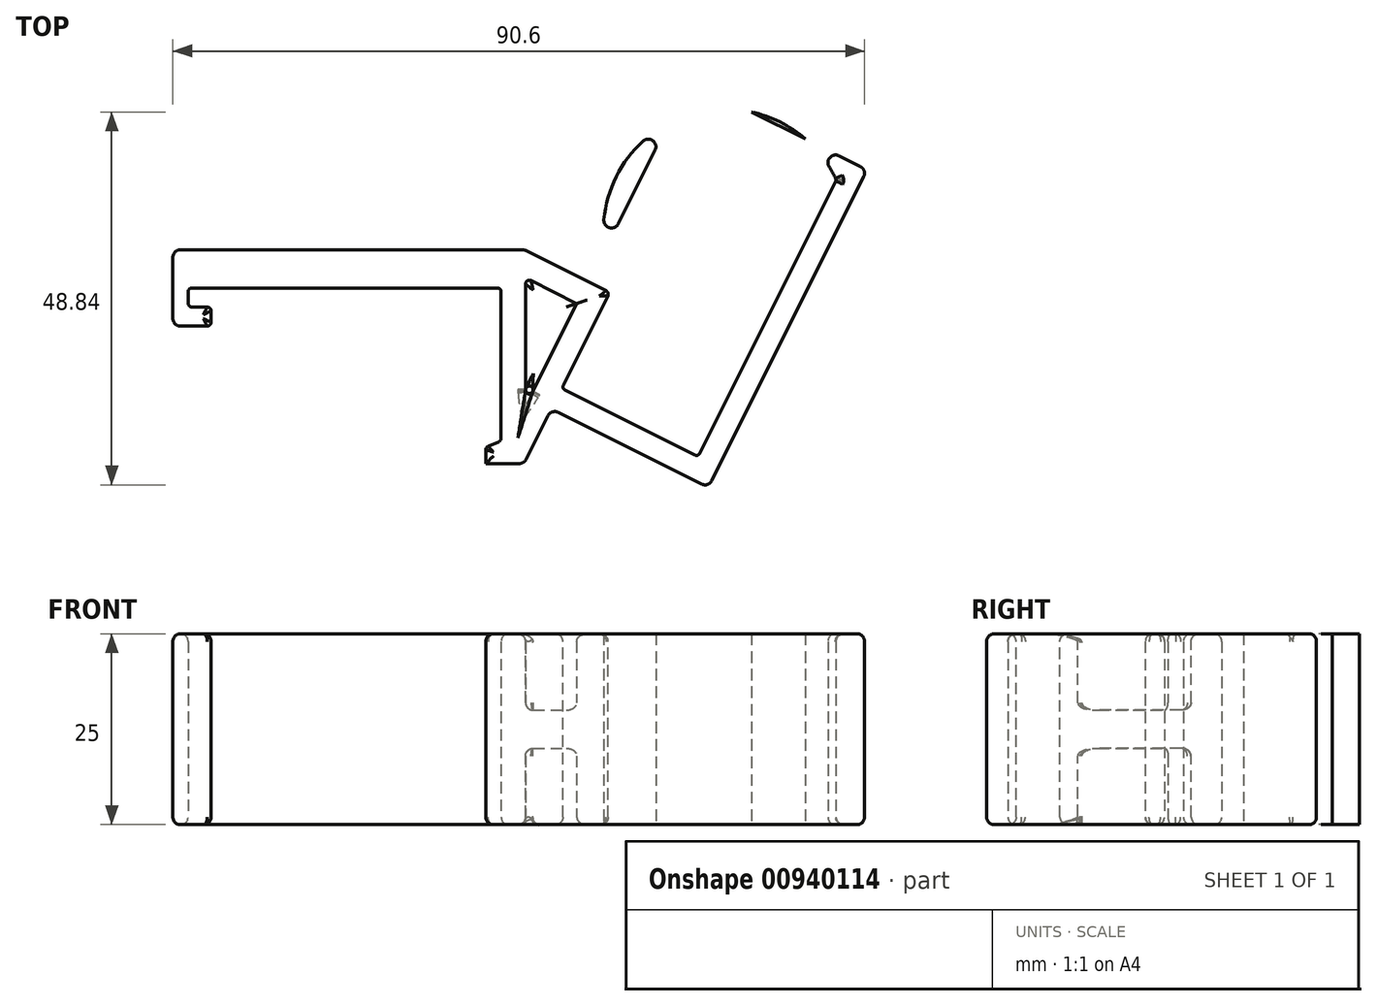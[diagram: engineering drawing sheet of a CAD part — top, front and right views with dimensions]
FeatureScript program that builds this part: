
annotation { "Feature Type Name" : "Feature", "Feature Type Description" : "" }
export const myFeature = defineFeature(function(context is Context, id is Id, definition is map)
    precondition{}
    {
        {
            var Q0;
            Q0=qCreatedBy(makeId("Top.planeOp"),FACE);
            var sketch = newSketch(context, id + "F0", { "sketchPlane" : qUnion([Q0])});
            skLineSegment(sketch, "E0.bottom", {"start": v(0, 0) * mm, "end": v(41, 0) * mm});
            skLineSegment(sketch, "E0.top", {"start": v(0, 2) * mm, "end": v(41, 2) * mm});
            skLineSegment(sketch, "E0.left", {"start": v(0, 0) * mm, "end": v(0, 2) * mm});
            skLineSegment(sketch, "E0.right", {"start": v(41, 0) * mm, "end": v(41, 2) * mm});
            skLineSegment(sketch, "E1.bottom", {"start": v(0, 2) * mm, "end": v(-2, 2) * mm});
            skLineSegment(sketch, "E1.top", {"start": v(0, -2.5) * mm, "end": v(-2, -2.5) * mm});
            skLineSegment(sketch, "E1.left", {"start": v(0, 2) * mm, "end": v(0, -2.5) * mm});
            skLineSegment(sketch, "E1.right", {"start": v(-2, 2) * mm, "end": v(-2, -2.5) * mm});
            skLineSegment(sketch, "E2.bottom", {"start": v(-2, -2.5) * mm, "end": v(3, -2.5) * mm});
            skLineSegment(sketch, "E2.top", {"start": v(-2, -5) * mm, "end": v(3, -5) * mm});
            skLineSegment(sketch, "E2.left", {"start": v(-2, -2.5) * mm, "end": v(-2, -5) * mm});
            skLineSegment(sketch, "E2.right", {"start": v(3, -2.5) * mm, "end": v(3, -5) * mm});
            skLineSegment(sketch, "E3.bottom", {"start": v(41, 2) * mm, "end": v(44, 2) * mm});
            skLineSegment(sketch, "E3.top", {"start": v(41, -23) * mm, "end": v(44, -23) * mm});
            skLineSegment(sketch, "E3.left", {"start": v(41, 2) * mm, "end": v(41, -23) * mm});
            skLineSegment(sketch, "E3.right", {"start": v(44, 2) * mm, "end": v(44, -23) * mm});
            skLineSegment(sketch, "E4.bottom", {"start": v(41, -23) * mm, "end": v(39, -23) * mm});
            skLineSegment(sketch, "E4.top", {"start": v(41, -20) * mm, "end": v(39, -20) * mm});
            skLineSegment(sketch, "E4.left", {"start": v(41, -23) * mm, "end": v(41, -20) * mm});
            skLineSegment(sketch, "E4.right", {"start": v(39, -23) * mm, "end": v(39, -20) * mm});
            skLineSegment(sketch, "E5.bottom", {"start": v(39, -23) * mm, "end": v(37.5, -23) * mm});
            skLineSegment(sketch, "E5.top", {"start": v(39, -13) * mm, "end": v(37.5, -13) * mm});
            skLineSegment(sketch, "E5.left", {"start": v(39, -23) * mm, "end": v(39, -13) * mm});
            skLineSegment(sketch, "E5.right", {"start": v(37.5, -23) * mm, "end": v(37.5, -13) * mm});
            skLineSegment(sketch, "E6.bottom", {"start": v(-2, 2) * mm, "end": v(44, 2) * mm});
            skLineSegment(sketch, "E6.top", {"start": v(-2, 5) * mm, "end": v(44, 5) * mm});
            skLineSegment(sketch, "E6.left", {"start": v(-2, 2) * mm, "end": v(-2, 5) * mm});
            skLineSegment(sketch, "E6.right", {"start": v(44, 2) * mm, "end": v(44, 5) * mm});
            skLineSegment(sketch, "E7", {"start": v(44, 5) * mm, "end": v(28, 14) * mm});
            skLineSegment(sketch, "E8", {"start": v(28, 14) * mm, "end": v(-2, 5) * mm});
            skLineSegment(sketch, "E9", {"start": v(28, 14) * mm, "end": v(28, 5) * mm});
            skLineSegment(sketch, "E10.bottom", {"start": v(37.5, -23) * mm, "end": v(39, -23) * mm});
            skLineSegment(sketch, "E10.top", {"start": v(37.5, -20) * mm, "end": v(39, -20) * mm});
            skLineSegment(sketch, "E10.left", {"start": v(37.5, -23) * mm, "end": v(37.5, -20) * mm});
            skLineSegment(sketch, "E11.bottom", {"start": v(44, 5) * mm, "end": v(28, 5) * mm});
            skLineSegment(sketch, "E11.top", {"start": v(44, 14) * mm, "end": v(28, 14) * mm});
            skLineSegment(sketch, "E11.left", {"start": v(44, 5) * mm, "end": v(44, 14) * mm});
            skLineSegment(sketch, "E11.right", {"start": v(28, 5) * mm, "end": v(28, 14) * mm});
            skLineSegment(sketch, "E12.bottom", {"start": v(-2, 5) * mm, "end": v(28, 5) * mm});
            skLineSegment(sketch, "E12.top", {"start": v(-2, 14) * mm, "end": v(28, 14) * mm});
            skLineSegment(sketch, "E12.left", {"start": v(-2, 5) * mm, "end": v(-2, 14) * mm});
            skLineSegment(sketch, "E13", {"start": v(44, -23) * mm, "end": v(55.2, -0.6) * mm});
            skLineSegment(sketch, "E14", {"start": v(37.5, -21.5) * mm, "end": v(41, -20) * mm});
            skLineSegment(sketch, "E15", {"start": v(44, 5) * mm, "end": v(55.2, -0.6) * mm});
            skLineSegment(sketch, "E16", {"start": v(57.86, -17.63) * mm, "end": v(70.39, 7.41) * mm});
            skCircle(sketch, "E17", {"center": v(70.39, 7.41) * mm, "radius": 16 * mm});
            skLineSegment(sketch, "E18", {"start": v(55.2, -0.6) * mm, "end": v(67.03, 23.06) * mm});
            skLineSegment(sketch, "E19", {"start": v(57.86, -17.63) * mm, "end": v(48.92, -13.16) * mm});
            skLineSegment(sketch, "E20", {"start": v(67.03, 23.06) * mm, "end": v(84.9, 14.12) * mm});
            skLineSegment(sketch, "E21", {"start": v(84.9, 14.12) * mm, "end": v(66.8, -22.1) * mm});
            skLineSegment(sketch, "E22", {"start": v(66.8, -22.1) * mm, "end": v(57.86, -17.63) * mm});
            skLineSegment(sketch, "E23", {"start": v(47.58, -15.84) * mm, "end": v(68.15, -26.13) * mm});
            skLineSegment(sketch, "E24", {"start": v(68.15, -26.13) * mm, "end": v(88.94, 15.46) * mm});
            skLineSegment(sketch, "E25", {"start": v(88.94, 15.46) * mm, "end": v(65.69, 27.09) * mm});
            skPoint(sketch, "E26", {"position": v(55.2, -0.6) * mm});
            skPoint(sketch, "E27", {"position": v(52.52, 0.74) * mm});
            skLineSegment(sketch, "E28", {"start": v(52.52, 0.74) * mm, "end": v(65.69, 27.09) * mm});
            skSolve(sketch);
        }
        {
            var Q0;
            Q0=makeQuery(id+"F0.imprint","IMPRINT",FACE,{"disambiguationData":[TD([[makeQuery(id+"F0.imprint","IMPRINT",EDGE,{"derivedFrom":sQuery(id+"F0.wireOp",EDGE,"E2.top")}),1.0]])]});
            var Q1;
            Q1=makeQuery(id+"F0.imprint","IMPRINT",FACE,{"disambiguationData":[TD([[makeQuery(id+"F0.imprint","IMPRINT",EDGE,{"derivedFrom":sQuery(id+"F0.wireOp",EDGE,"E4.bottom")}),-1.0]])]});
            var Q2;
            Q2=makeQuery(id+"F0.imprint","IMPRINT",FACE,{"disambiguationData":[TD([[makeQuery(id+"F0.imprint","IMPRINT",EDGE,{"derivedFrom":sQuery(id+"F0.wireOp",EDGE,"E10.bottom")}),1.0]])]});
            var Q3;
            {var subQ0=sQuery(id+"F0.wireOp",EDGE,"E6.left");Q3=makeQuery(id+"F0.imprint","IMPRINT",FACE,{"disambiguationData":[TD([[makeQuery(id+"F0.imprint","IMPRINT",EDGE,{"derivedFrom":subQ0}),-1.0]])]});}
            var Q4;
            Q4=makeQuery(id+"F0.imprint","IMPRINT",FACE,{"disambiguationData":[TD([[makeQuery(id+"F0.imprint","IMPRINT",EDGE,{"derivedFrom":sQuery(id+"F0.wireOp",EDGE,"E3.right")}),1.0]])]});
            var Q5;
            Q5=makeQuery(id+"F0.imprint","IMPRINT",FACE,{"disambiguationData":[TD([[makeQuery(id+"F0.imprint","IMPRINT",EDGE,{"derivedFrom":sQuery(id+"F0.wireOp",EDGE,"E3.top")}),1.0]])]});
            var Q6;
            {var subQ4=sQuery(id+"F0.wireOp",EDGE,"JwhKLXGQ-pJKR-nMGy-SPGt-QLhxBQO2lQYZ");var subQ6=sQuery(id+"F0.wireOp",EDGE,"E13");var subQ7=makeQuery(id+"F0.imprint","INTERSECT",VERTEX,{"derivedFrom":[subQ4,subQ6]});Q6=makeQuery(id+"F0.imprint","IMPRINT",FACE,{"disambiguationData":[TD([[makeQuery(id+"F0.imprint","IMPRINT",EDGE,{"disambiguationData":[TD([[subQ7,1.0]])],"derivedFrom":subQ6}),1.0]])]});}
            var Q7;
            {var subQ3=sQuery(id+"F0.wireOp",EDGE,"E1.right");Q7=makeQuery(id+"F0.imprint","IMPRINT",FACE,{"disambiguationData":[TD([[makeQuery(id+"F0.imprint","IMPRINT",EDGE,{"derivedFrom":subQ3}),1.0]])]});}
            var Q8;
            {var subQ0=sQuery(id+"F0.wireOp",EDGE,"E0.bottom");Q8=makeQuery(id+"F0.imprint","IMPRINT",FACE,{"disambiguationData":[TD([[makeQuery(id+"F0.imprint","IMPRINT",EDGE,{"derivedFrom":subQ0}),1.0]])]});}
            var Q9;
            {var subQ4=sQuery(id+"F0.wireOp",EDGE,"E19");Q9=makeQuery(id+"F0.imprint","IMPRINT",FACE,{"disambiguationData":[TD([[makeQuery(id+"F0.imprint","IMPRINT",EDGE,{"derivedFrom":subQ4}),1.0]])]});}
            var Q10;
            {var subQ1=sQuery(id+"F0.wireOp",EDGE,"E17");var subQ3=sQuery(id+"F0.wireOp",EDGE,"E24");var subQ5=makeQuery(id+"F0.imprint","INTERSECT",VERTEX,{"disambiguationData":[OD(1.0)],"derivedFrom":[subQ1,subQ3]});Q10=makeQuery(id+"F0.imprint","IMPRINT",FACE,{"disambiguationData":[TD([[makeQuery(id+"F0.imprint","IMPRINT",EDGE,{"disambiguationData":[TD([[subQ5,1.0]])],"derivedFrom":subQ1}),1.0]])]});}
            var Q11;
            {var subQ2=sQuery(id+"F0.wireOp",EDGE,"E24");var subQ4=sQuery(id+"F0.wireOp",EDGE,"E25");var subQ5=makeQuery(id+"F0.imprint","INTERSECT",VERTEX,{"derivedFrom":[subQ2,subQ4]});Q11=makeQuery(id+"F0.imprint","IMPRINT",FACE,{"disambiguationData":[TD([[makeQuery(id+"F0.imprint","IMPRINT",EDGE,{"disambiguationData":[TD([[subQ5,1.0]])],"derivedFrom":subQ2}),1.0]])]});}
            var Q12;
            {var subQ1=sQuery(id+"F0.wireOp",EDGE,"E17");var subQ3=sQuery(id+"F0.wireOp",EDGE,"E25");var subQ5=makeQuery(id+"F0.imprint","INTERSECT",VERTEX,{"disambiguationData":[OD(1.0)],"derivedFrom":[subQ1,subQ3]});Q12=makeQuery(id+"F0.imprint","IMPRINT",FACE,{"disambiguationData":[TD([[makeQuery(id+"F0.imprint","IMPRINT",EDGE,{"disambiguationData":[TD([[subQ5,-1.0]])],"derivedFrom":subQ1}),1.0]])]});}
            var Q13;
            {var subQ3=sQuery(id+"F0.wireOp",EDGE,"E17");var subQ8=sQuery(id+"F0.wireOp",EDGE,"E25");var subQ10=makeQuery(id+"F0.imprint","INTERSECT",VERTEX,{"disambiguationData":[OD(1.0)],"derivedFrom":[subQ3,subQ8]});Q13=makeQuery(id+"F0.imprint","IMPRINT",FACE,{"disambiguationData":[TD([[makeQuery(id+"F0.imprint","IMPRINT",EDGE,{"disambiguationData":[TD([[subQ10,-1.0]])],"derivedFrom":subQ3}),-1.0]])]});}
            var Q14;
            {var subQ0=sQuery(id+"F0.wireOp",EDGE,"E28");var subQ1=sQuery(id+"F0.wireOp",EDGE,"E17");var subQ2=makeQuery(id+"F0.imprint","INTERSECT",VERTEX,{"disambiguationData":[OD(0.0)],"derivedFrom":[subQ1,subQ0]});Q14=makeQuery(id+"F0.imprint","IMPRINT",FACE,{"disambiguationData":[TD([[makeQuery(id+"F0.imprint","IMPRINT",EDGE,{"disambiguationData":[TD([[subQ2,1.0]])],"derivedFrom":subQ1}),1.0]])]});}
            var Q15;
            {var subQ3=sQuery(id+"F0.wireOp",EDGE,"E28");var subQ5=sQuery(id+"F0.wireOp",EDGE,"E17");var subQ6=makeQuery(id+"F0.imprint","INTERSECT",VERTEX,{"disambiguationData":[OD(1.0)],"derivedFrom":[subQ5,subQ3]});Q15=makeQuery(id+"F0.imprint","IMPRINT",FACE,{"disambiguationData":[TD([[makeQuery(id+"F0.imprint","IMPRINT",EDGE,{"disambiguationData":[TD([[subQ6,-1.0]])],"derivedFrom":subQ5}),-1.0]])]});}
            extrude(context, id + "F1", {"entities" : qUnion([Q0, Q1, Q2, Q3, Q4, Q5, Q6, Q7, Q8, Q9, Q10, Q11, Q12, Q13, Q14, Q15]), "depth" : 12.5 * mm, "offsetDistance" : 25 * mm, "hasSecondDirection" : true, "secondDirectionOppositeDirection" : true, "secondDirectionDepth" : 12.5 * mm});
        }
        {
            var Q0;
            Q0=makeQuery(id+"F1.opExtrude","CAP_FACE",FACE,{"disambiguationData":[OSD([sQuery(id+"F0.wireOp",EDGE,"E1.left"),sQuery(id+"F0.wireOp",EDGE,"E1.right"),sQuery(id+"F0.wireOp",EDGE,"E2.bottom"),sQuery(id+"F0.wireOp",EDGE,"E2.top"),sQuery(id+"F0.wireOp",EDGE,"E2.left"),sQuery(id+"F0.wireOp",EDGE,"E2.right"),sQuery(id+"F0.wireOp",EDGE,"E3.top"),sQuery(id+"F0.wireOp",EDGE,"E3.left"),sQuery(id+"F0.wireOp",EDGE,"E4.bottom"),sQuery(id+"F0.wireOp",EDGE,"E4.top"),sQuery(id+"F0.wireOp",EDGE,"E6.bottom"),sQuery(id+"F0.wireOp",EDGE,"E6.left"),sQuery(id+"F0.wireOp",EDGE,"E7"),sQuery(id+"F0.wireOp",EDGE,"E8"),sQuery(id+"F0.wireOp",EDGE,"E10.bottom"),sQuery(id+"F0.wireOp",EDGE,"E10.top"),sQuery(id+"F0.wireOp",EDGE,"E10.left"),sQuery(id+"F0.wireOp",EDGE,"JwhKLXGQ-pJKR-nMGy-SPGt-QLhxBQO2lQYZ"),sQuery(id+"F0.wireOp",EDGE,"E13")])],"isStart":false});
            var Q1;
            Q1=makeQuery(id+"F1.opExtrude","CAP_FACE",FACE,{"disambiguationData":[OSD([sQuery(id+"F0.wireOp",EDGE,"E1.left"),sQuery(id+"F0.wireOp",EDGE,"E1.right"),sQuery(id+"F0.wireOp",EDGE,"E2.bottom"),sQuery(id+"F0.wireOp",EDGE,"E2.top"),sQuery(id+"F0.wireOp",EDGE,"E2.left"),sQuery(id+"F0.wireOp",EDGE,"E2.right"),sQuery(id+"F0.wireOp",EDGE,"E3.top"),sQuery(id+"F0.wireOp",EDGE,"E3.left"),sQuery(id+"F0.wireOp",EDGE,"E4.bottom"),sQuery(id+"F0.wireOp",EDGE,"E4.top"),sQuery(id+"F0.wireOp",EDGE,"E6.bottom"),sQuery(id+"F0.wireOp",EDGE,"E6.left"),sQuery(id+"F0.wireOp",EDGE,"E7"),sQuery(id+"F0.wireOp",EDGE,"E8"),sQuery(id+"F0.wireOp",EDGE,"E10.bottom"),sQuery(id+"F0.wireOp",EDGE,"E10.top"),sQuery(id+"F0.wireOp",EDGE,"E10.left"),sQuery(id+"F0.wireOp",EDGE,"JwhKLXGQ-pJKR-nMGy-SPGt-QLhxBQO2lQYZ"),sQuery(id+"F0.wireOp",EDGE,"E13")])],"isStart":true});
            shell(context, id + "F2", {"entities" : qUnion([Q0, Q1]), "thickness" : 3.2 * mm});
        }
        {
            var Q0;
            {var subQ0=sQuery(id+"F0.wireOp",EDGE,"E6.left");Q0=makeQuery(id+"F0.imprint","IMPRINT",FACE,{"disambiguationData":[TD([[makeQuery(id+"F0.imprint","IMPRINT",EDGE,{"derivedFrom":subQ0}),-1.0]])]});}
            var Q1;
            {var subQ4=sQuery(id+"F0.wireOp",EDGE,"JwhKLXGQ-pJKR-nMGy-SPGt-QLhxBQO2lQYZ");var subQ6=sQuery(id+"F0.wireOp",EDGE,"E13");var subQ7=makeQuery(id+"F0.imprint","INTERSECT",VERTEX,{"derivedFrom":[subQ4,subQ6]});Q1=makeQuery(id+"F0.imprint","IMPRINT",FACE,{"disambiguationData":[TD([[makeQuery(id+"F0.imprint","IMPRINT",EDGE,{"disambiguationData":[TD([[subQ7,1.0]])],"derivedFrom":subQ6}),1.0]])]});}
            var Q2;
            {var subQ0=sQuery(id+"F0.wireOp",EDGE,"E3.right");Q2=makeQuery(id+"F0.imprint","IMPRINT",FACE,{"disambiguationData":[TD([[makeQuery(id+"F0.imprint","IMPRINT",EDGE,{"derivedFrom":subQ0}),1.0]])]});}
            extrude(context, id + "F3", {"entities" : qUnion([Q0, Q1, Q2]), "operationType" : NewBodyOperationType.ADD, "depth" : 2.5 * mm, "offsetDistance" : 25 * mm, "hasSecondDirection" : true, "secondDirectionOppositeDirection" : true, "secondDirectionDepth" : 2.5 * mm});
        }
        {
            var Q0;
            Q0=makeQuery(id+"F1.opExtrude","CAP_FACE",FACE,{"disambiguationData":[OSD([sQuery(id+"F0.wireOp",EDGE,"E0.bottom"),sQuery(id+"F0.wireOp",EDGE,"E1.left"),sQuery(id+"F0.wireOp",EDGE,"E1.right"),sQuery(id+"F0.wireOp",EDGE,"E2.bottom"),sQuery(id+"F0.wireOp",EDGE,"E2.top"),sQuery(id+"F0.wireOp",EDGE,"E2.left"),sQuery(id+"F0.wireOp",EDGE,"E2.right"),sQuery(id+"F0.wireOp",EDGE,"E3.top"),sQuery(id+"F0.wireOp",EDGE,"E3.left"),sQuery(id+"F0.wireOp",EDGE,"E4.bottom"),sQuery(id+"F0.wireOp",EDGE,"E6.left"),sQuery(id+"F0.wireOp",EDGE,"E10.bottom"),sQuery(id+"F0.wireOp",EDGE,"E10.left"),sQuery(id+"F0.wireOp",EDGE,"E11.bottom"),sQuery(id+"F0.wireOp",EDGE,"E12.bottom"),sQuery(id+"F0.wireOp",EDGE,"E13"),sQuery(id+"F0.wireOp",EDGE,"E14"),sQuery(id+"F0.wireOp",EDGE,"E15"),sQuery(id+"F0.wireOp",EDGE,"E18"),sQuery(id+"F0.wireOp",EDGE,"E19"),sQuery(id+"F0.wireOp",EDGE,"E20"),sQuery(id+"F0.wireOp",EDGE,"E21"),sQuery(id+"F0.wireOp",EDGE,"E22"),sQuery(id+"F0.wireOp",EDGE,"E23"),sQuery(id+"F0.wireOp",EDGE,"E24"),sQuery(id+"F0.wireOp",EDGE,"E25"),sQuery(id+"F0.wireOp",EDGE,"E28")])],"isStart":false});
            var Q1;
            Q1=makeQuery(id+"F1.opExtrude","CAP_FACE",FACE,{"disambiguationData":[OSD([sQuery(id+"F0.wireOp",EDGE,"E0.bottom"),sQuery(id+"F0.wireOp",EDGE,"E1.left"),sQuery(id+"F0.wireOp",EDGE,"E1.right"),sQuery(id+"F0.wireOp",EDGE,"E2.bottom"),sQuery(id+"F0.wireOp",EDGE,"E2.top"),sQuery(id+"F0.wireOp",EDGE,"E2.left"),sQuery(id+"F0.wireOp",EDGE,"E2.right"),sQuery(id+"F0.wireOp",EDGE,"E3.top"),sQuery(id+"F0.wireOp",EDGE,"E3.left"),sQuery(id+"F0.wireOp",EDGE,"E4.bottom"),sQuery(id+"F0.wireOp",EDGE,"E6.left"),sQuery(id+"F0.wireOp",EDGE,"E10.bottom"),sQuery(id+"F0.wireOp",EDGE,"E10.left"),sQuery(id+"F0.wireOp",EDGE,"E11.bottom"),sQuery(id+"F0.wireOp",EDGE,"E12.bottom"),sQuery(id+"F0.wireOp",EDGE,"E13"),sQuery(id+"F0.wireOp",EDGE,"E14"),sQuery(id+"F0.wireOp",EDGE,"E15"),sQuery(id+"F0.wireOp",EDGE,"E18"),sQuery(id+"F0.wireOp",EDGE,"E19"),sQuery(id+"F0.wireOp",EDGE,"E20"),sQuery(id+"F0.wireOp",EDGE,"E21"),sQuery(id+"F0.wireOp",EDGE,"E22"),sQuery(id+"F0.wireOp",EDGE,"E23"),sQuery(id+"F0.wireOp",EDGE,"E24"),sQuery(id+"F0.wireOp",EDGE,"E25"),sQuery(id+"F0.wireOp",EDGE,"E28")])],"isStart":true});
            var Q2;
            Q2=makeQuery(id+"F1.opExtrude","SWEPT_EDGE",EDGE,{"disambiguationData":[OSD([sQuery(id+"F0.wireOp",EDGE,"E6.right"),sQuery(id+"F0.wireOp",EDGE,"E7"),sQuery(id+"F0.wireOp",EDGE,"E11.bottom"),sQuery(id+"F0.wireOp",EDGE,"E11.left"),sQuery(id+"F0.wireOp",EDGE,"E15")])]});
            var Q3;
            Q3=makeQuery(id+"F1.opExtrude","SWEPT_EDGE",EDGE,{"disambiguationData":[OSD([sQuery(id+"F0.wireOp",EDGE,"E15"),sQuery(id+"F0.wireOp",EDGE,"E28")])]});
            var Q4;
            Q4=makeQuery(id+"F1.opExtrude","SWEPT_EDGE",EDGE,{"disambiguationData":[OSD([sQuery(id+"F0.wireOp",EDGE,"E6.left"),sQuery(id+"F0.wireOp",EDGE,"E8"),sQuery(id+"F0.wireOp",EDGE,"E12.bottom"),sQuery(id+"F0.wireOp",EDGE,"E12.left")])]});
            var Q5;
            Q5=makeQuery(id+"F1.opExtrude","SWEPT_EDGE",EDGE,{"disambiguationData":[OSD([sQuery(id+"F0.wireOp",EDGE,"E2.top"),sQuery(id+"F0.wireOp",EDGE,"E2.left")])]});
            var Q6;
            Q6=makeQuery(id+"F1.opExtrude","SWEPT_EDGE",EDGE,{"disambiguationData":[OSD([sQuery(id+"F0.wireOp",EDGE,"E25"),sQuery(id+"F0.wireOp",EDGE,"E28")])]});
            var Q7;
            Q7=makeQuery(id+"F1.opExtrude","SWEPT_EDGE",EDGE,{"disambiguationData":[OSD([sQuery(id+"F0.wireOp",EDGE,"E24"),sQuery(id+"F0.wireOp",EDGE,"E25")])]});
            var Q8;
            Q8=makeQuery(id+"F1.opExtrude","SWEPT_EDGE",EDGE,{"disambiguationData":[OSD([sQuery(id+"F0.wireOp",EDGE,"E23"),sQuery(id+"F0.wireOp",EDGE,"E24")])]});
            var Q9;
            Q9=makeQuery(id+"F1.opExtrude","SWEPT_EDGE",EDGE,{"disambiguationData":[OSD([sQuery(id+"F0.wireOp",EDGE,"E13"),sQuery(id+"F0.wireOp",EDGE,"E23")])]});
            var Q10;
            Q10=makeQuery(id+"F1.opExtrude","SWEPT_EDGE",EDGE,{"disambiguationData":[OSD([sQuery(id+"F0.wireOp",EDGE,"E3.top"),sQuery(id+"F0.wireOp",EDGE,"E3.right"),sQuery(id+"F0.wireOp",EDGE,"E13")])]});
            var Q11;
            Q11=makeQuery(id+"F3.opExtrude","CAP_FACE",FACE,{"disambiguationData":[OSD([sQuery(id+"F0.wireOp",EDGE,"E3.right"),sQuery(id+"F0.wireOp",EDGE,"E6.bottom"),sQuery(id+"F0.wireOp",EDGE,"E6.left"),sQuery(id+"F0.wireOp",EDGE,"E11.bottom"),sQuery(id+"F0.wireOp",EDGE,"E12.bottom"),sQuery(id+"F0.wireOp",EDGE,"E13"),sQuery(id+"F0.wireOp",EDGE,"E15")])],"isStart":true});
            var Q12;
            Q12=makeQuery(id+"F3.opExtrude","CAP_FACE",FACE,{"disambiguationData":[OSD([sQuery(id+"F0.wireOp",EDGE,"E3.right"),sQuery(id+"F0.wireOp",EDGE,"E6.bottom"),sQuery(id+"F0.wireOp",EDGE,"E6.left"),sQuery(id+"F0.wireOp",EDGE,"E11.bottom"),sQuery(id+"F0.wireOp",EDGE,"E12.bottom"),sQuery(id+"F0.wireOp",EDGE,"E13"),sQuery(id+"F0.wireOp",EDGE,"E15")])],"isStart":false});
            fillet(context, id + "F4", {"entities" : qUnion([Q0, Q1, Q2, Q3, Q4, Q5, Q6, Q7, Q8, Q9, Q10, Q11, Q12]), "radius" : 1 * mm, "tangentPropagation" : true, "allowEdgeOverflow" : false});
        }
        {
            var Q0;
            {var subQ0=sQuery(id+"F0.wireOp",EDGE,"E18");var subQ1=sQuery(id+"F0.wireOp",EDGE,"E15");var subQ2=sQuery(id+"F0.wireOp",EDGE,"E13");var subQ3=sQuery(id+"F0.wireOp",EDGE,"E12.bottom");var subQ4=sQuery(id+"F0.wireOp",EDGE,"E11.bottom");var subQ5=sQuery(id+"F0.wireOp",EDGE,"E6.left");var subQ6=sQuery(id+"F0.wireOp",EDGE,"E3.left");Q0=makeQuery(id+"F3.boolean.opBoolean","SPLIT",EDGE,{"disambiguationData":[TD([makeQuery(id+"F3.opExtrude","CAP_FACE",FACE,{"disambiguationData":[OSD([sQuery(id+"F0.wireOp",EDGE,"E3.right"),sQuery(id+"F0.wireOp",EDGE,"E6.bottom"),subQ5,subQ4,subQ3,subQ2,subQ1])],"isStart":false})])],"derivedFrom":makeQuery(id+"F2.opShell","TWEAK_EDGE",EDGE,{"derivedFrom":[makeQuery(id+"F1.opExtrude","SWEPT_FACE",FACE,{"disambiguationData":[OSD([subQ6])]}),makeQuery(id+"F1.opExtrude","SWEPT_FACE",FACE,{"disambiguationData":[OSD([subQ2])]}),makeQuery(id+"F1.opExtrude","SWEPT_FACE",FACE,{"disambiguationData":[OSD([subQ2,subQ0])]})]})});}
            var Q1;
            {var subQ0=sQuery(id+"F0.wireOp",EDGE,"E15");var subQ1=sQuery(id+"F0.wireOp",EDGE,"E13");var subQ2=sQuery(id+"F0.wireOp",EDGE,"E12.bottom");var subQ3=sQuery(id+"F0.wireOp",EDGE,"E11.bottom");var subQ4=sQuery(id+"F0.wireOp",EDGE,"E6.left");var subQ5=sQuery(id+"F0.wireOp",EDGE,"E3.left");Q1=makeQuery(id+"F3.boolean.opBoolean","SPLIT",EDGE,{"disambiguationData":[TD([makeQuery(id+"F3.opExtrude","CAP_FACE",FACE,{"disambiguationData":[OSD([sQuery(id+"F0.wireOp",EDGE,"E3.right"),sQuery(id+"F0.wireOp",EDGE,"E6.bottom"),subQ4,subQ3,subQ2,subQ1,subQ0])],"isStart":false})])],"derivedFrom":makeQuery(id+"F2.opShell","TWEAK_EDGE",EDGE,{"derivedFrom":[makeQuery(id+"F1.opExtrude","SWEPT_FACE",FACE,{"disambiguationData":[OSD([subQ5])]}),makeQuery(id+"F1.opExtrude","SWEPT_FACE",FACE,{"disambiguationData":[OSD([subQ0])]})]})});}
            var Q2;
            {var subQ0=sQuery(id+"F0.wireOp",EDGE,"E18");var subQ1=sQuery(id+"F0.wireOp",EDGE,"E15");var subQ2=sQuery(id+"F0.wireOp",EDGE,"E13");var subQ3=sQuery(id+"F0.wireOp",EDGE,"E12.bottom");var subQ4=sQuery(id+"F0.wireOp",EDGE,"E11.bottom");var subQ5=sQuery(id+"F0.wireOp",EDGE,"E6.left");Q2=makeQuery(id+"F3.boolean.opBoolean","SPLIT",EDGE,{"disambiguationData":[TD([makeQuery(id+"F3.opExtrude","CAP_FACE",FACE,{"disambiguationData":[OSD([sQuery(id+"F0.wireOp",EDGE,"E3.right"),sQuery(id+"F0.wireOp",EDGE,"E6.bottom"),subQ5,subQ4,subQ3,subQ2,subQ1])],"isStart":false})])],"derivedFrom":makeQuery(id+"F2.opShell","TWEAK_EDGE",EDGE,{"derivedFrom":[makeQuery(id+"F1.opExtrude","SWEPT_FACE",FACE,{"disambiguationData":[OSD([subQ2])]}),makeQuery(id+"F1.opExtrude","SWEPT_FACE",FACE,{"disambiguationData":[OSD([subQ2,subQ0])]}),makeQuery(id+"F1.opExtrude","SWEPT_FACE",FACE,{"disambiguationData":[OSD([subQ1])]})]})});}
            var Q3;
            Q3=makeQuery(id+"F1.opExtrude","SWEPT_EDGE",EDGE,{"disambiguationData":[OSD([sQuery(id+"F0.wireOp",EDGE,"E0.bottom"),sQuery(id+"F0.wireOp",EDGE,"E3.left")])]});
            var Q4;
            Q4=makeQuery(id+"F1.opExtrude","SWEPT_EDGE",EDGE,{"disambiguationData":[OSD([sQuery(id+"F0.wireOp",EDGE,"E3.left"),sQuery(id+"F0.wireOp",EDGE,"E4.top"),sQuery(id+"F0.wireOp",EDGE,"E4.left"),sQuery(id+"F0.wireOp",EDGE,"E14")])]});
            var Q5;
            Q5=makeQuery(id+"F1.opExtrude","SWEPT_EDGE",EDGE,{"disambiguationData":[OSD([sQuery(id+"F0.wireOp",EDGE,"E10.bottom"),sQuery(id+"F0.wireOp",EDGE,"E10.left")])]});
            var Q6;
            Q6=makeQuery(id+"F1.opExtrude","SWEPT_EDGE",EDGE,{"disambiguationData":[OSD([sQuery(id+"F0.wireOp",EDGE,"E10.left"),sQuery(id+"F0.wireOp",EDGE,"E14")])]});
            var Q7;
            Q7=makeQuery(id+"F1.opExtrude","SWEPT_EDGE",EDGE,{"disambiguationData":[OSD([sQuery(id+"F0.wireOp",EDGE,"E17"),sQuery(id+"F0.wireOp",EDGE,"E20"),sQuery(id+"F0.wireOp",EDGE,"E21")])]});
            var Q8;
            Q8=makeQuery(id+"F1.opExtrude","SWEPT_EDGE",EDGE,{"disambiguationData":[OSD([sQuery(id+"F0.wireOp",EDGE,"E13"),sQuery(id+"F0.wireOp",EDGE,"E19")])]});
            var Q9;
            Q9=makeQuery(id+"F1.opExtrude","SWEPT_EDGE",EDGE,{"disambiguationData":[OSD([sQuery(id+"F0.wireOp",EDGE,"E18"),sQuery(id+"F0.wireOp",EDGE,"E20")])]});
            var Q10;
            Q10=makeQuery(id+"F1.opExtrude","SWEPT_EDGE",EDGE,{"disambiguationData":[OSD([sQuery(id+"F0.wireOp",EDGE,"E21"),sQuery(id+"F0.wireOp",EDGE,"E22")])]});
            var Q11;
            Q11=makeQuery(id+"F1.opExtrude","SWEPT_EDGE",EDGE,{"disambiguationData":[OSD([sQuery(id+"F0.wireOp",EDGE,"E0.bottom"),sQuery(id+"F0.wireOp",EDGE,"E1.left")])]});
            var Q12;
            Q12=makeQuery(id+"F1.opExtrude","SWEPT_EDGE",EDGE,{"disambiguationData":[OSD([sQuery(id+"F0.wireOp",EDGE,"E2.top"),sQuery(id+"F0.wireOp",EDGE,"E2.right")])]});
            var Q13;
            Q13=makeQuery(id+"F1.opExtrude","SWEPT_EDGE",EDGE,{"disambiguationData":[OSD([sQuery(id+"F0.wireOp",EDGE,"E2.bottom"),sQuery(id+"F0.wireOp",EDGE,"E2.right")])]});
            var Q14;
            Q14=makeQuery(id+"F1.opExtrude","SWEPT_EDGE",EDGE,{"disambiguationData":[OSD([sQuery(id+"F0.wireOp",EDGE,"E1.left"),sQuery(id+"F0.wireOp",EDGE,"E2.bottom")])]});
            var Q15;
            {var subQ0=sQuery(id+"F0.wireOp",EDGE,"E18");var subQ1=sQuery(id+"F0.wireOp",EDGE,"E15");var subQ2=sQuery(id+"F0.wireOp",EDGE,"E13");var subQ3=sQuery(id+"F0.wireOp",EDGE,"E12.bottom");var subQ4=sQuery(id+"F0.wireOp",EDGE,"E11.bottom");var subQ5=sQuery(id+"F0.wireOp",EDGE,"E6.left");Q15=makeQuery(id+"F3.boolean.opBoolean","SPLIT",EDGE,{"disambiguationData":[TD([makeQuery(id+"F3.opExtrude","CAP_FACE",FACE,{"disambiguationData":[OSD([sQuery(id+"F0.wireOp",EDGE,"E3.right"),sQuery(id+"F0.wireOp",EDGE,"E6.bottom"),subQ5,subQ4,subQ3,subQ2,subQ1])],"isStart":true})])],"derivedFrom":makeQuery(id+"F2.opShell","TWEAK_EDGE",EDGE,{"derivedFrom":[makeQuery(id+"F1.opExtrude","SWEPT_FACE",FACE,{"disambiguationData":[OSD([subQ2])]}),makeQuery(id+"F1.opExtrude","SWEPT_FACE",FACE,{"disambiguationData":[OSD([subQ2,subQ0])]}),makeQuery(id+"F1.opExtrude","SWEPT_FACE",FACE,{"disambiguationData":[OSD([subQ1])]})]})});}
            var Q16;
            {var subQ0=sQuery(id+"F0.wireOp",EDGE,"E18");var subQ1=sQuery(id+"F0.wireOp",EDGE,"E15");var subQ2=sQuery(id+"F0.wireOp",EDGE,"E13");var subQ3=sQuery(id+"F0.wireOp",EDGE,"E12.bottom");var subQ4=sQuery(id+"F0.wireOp",EDGE,"E11.bottom");var subQ5=sQuery(id+"F0.wireOp",EDGE,"E6.left");var subQ6=sQuery(id+"F0.wireOp",EDGE,"E3.left");Q16=makeQuery(id+"F3.boolean.opBoolean","SPLIT",EDGE,{"disambiguationData":[TD([makeQuery(id+"F3.opExtrude","CAP_FACE",FACE,{"disambiguationData":[OSD([sQuery(id+"F0.wireOp",EDGE,"E3.right"),sQuery(id+"F0.wireOp",EDGE,"E6.bottom"),subQ5,subQ4,subQ3,subQ2,subQ1])],"isStart":true})])],"derivedFrom":makeQuery(id+"F2.opShell","TWEAK_EDGE",EDGE,{"derivedFrom":[makeQuery(id+"F1.opExtrude","SWEPT_FACE",FACE,{"disambiguationData":[OSD([subQ6])]}),makeQuery(id+"F1.opExtrude","SWEPT_FACE",FACE,{"disambiguationData":[OSD([subQ2])]}),makeQuery(id+"F1.opExtrude","SWEPT_FACE",FACE,{"disambiguationData":[OSD([subQ2,subQ0])]})]})});}
            var Q17;
            {var subQ0=sQuery(id+"F0.wireOp",EDGE,"E15");var subQ1=sQuery(id+"F0.wireOp",EDGE,"E13");var subQ2=sQuery(id+"F0.wireOp",EDGE,"E12.bottom");var subQ3=sQuery(id+"F0.wireOp",EDGE,"E11.bottom");var subQ4=sQuery(id+"F0.wireOp",EDGE,"E6.left");var subQ5=sQuery(id+"F0.wireOp",EDGE,"E3.left");Q17=makeQuery(id+"F3.boolean.opBoolean","SPLIT",EDGE,{"disambiguationData":[TD([makeQuery(id+"F3.opExtrude","CAP_FACE",FACE,{"disambiguationData":[OSD([sQuery(id+"F0.wireOp",EDGE,"E3.right"),sQuery(id+"F0.wireOp",EDGE,"E6.bottom"),subQ4,subQ3,subQ2,subQ1,subQ0])],"isStart":true})])],"derivedFrom":makeQuery(id+"F2.opShell","TWEAK_EDGE",EDGE,{"derivedFrom":[makeQuery(id+"F1.opExtrude","SWEPT_FACE",FACE,{"disambiguationData":[OSD([subQ5])]}),makeQuery(id+"F1.opExtrude","SWEPT_FACE",FACE,{"disambiguationData":[OSD([subQ0])]})]})});}
            fillet(context, id + "F5", {"entities" : qUnion([Q0, Q1, Q2, Q3, Q4, Q5, Q6, Q7, Q8, Q9, Q10, Q11, Q12, Q13, Q14, Q15, Q16, Q17]), "radius" : 0.5 * mm, "tangentPropagation" : true, "allowEdgeOverflow" : false});
        }
    });
